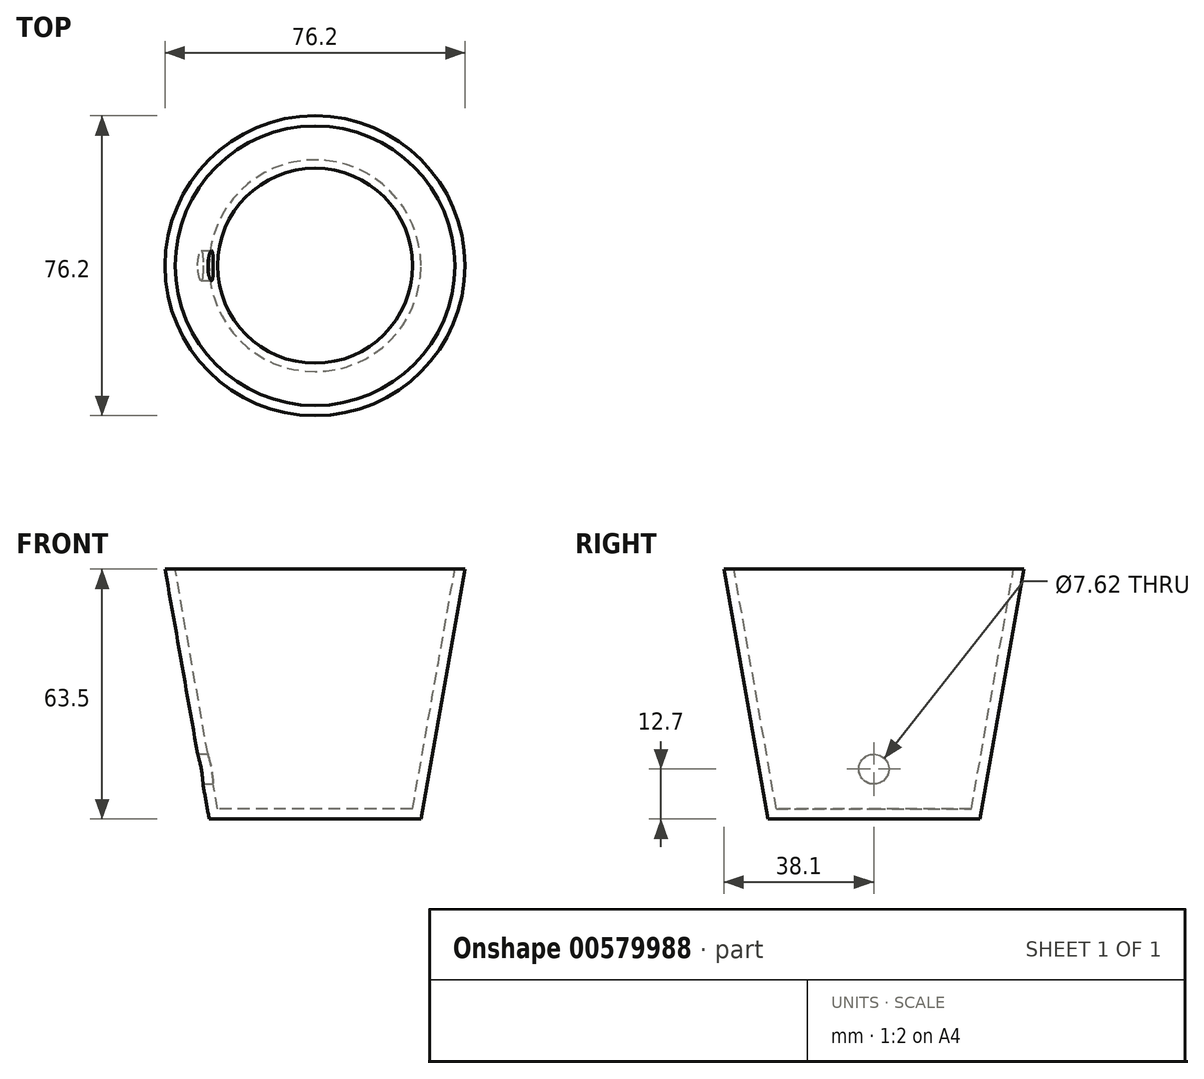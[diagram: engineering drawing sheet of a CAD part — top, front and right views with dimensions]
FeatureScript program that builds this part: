
annotation { "Feature Type Name" : "Feature", "Feature Type Description" : "" }
export const myFeature = defineFeature(function(context is Context, id is Id, definition is map)
    precondition{}
    {
        {
            var Q0;
            Q0=qCreatedBy(makeId("Front.planeOp"),FACE);
            var sketch = newSketch(context, id + "F0", { "sketchPlane" : qUnion([Q0])});
            skLineSegment(sketch, "E0", {"start": v(0, 63.5) * mm, "end": v(-38.1, 63.5) * mm});
            skLineSegment(sketch, "E1", {"start": v(-38.1, 63.5) * mm, "end": v(-26.9, 0) * mm});
            skLineSegment(sketch, "E2", {"start": v(-26.9, 0) * mm, "end": v(0, 0) * mm});
            skLineSegment(sketch, "E3", {"start": v(0, 0) * mm, "end": v(0, 63.5) * mm});
            skSolve(sketch);
        }
        {
            var Q0;
            Q0=makeQuery(id+"F0.imprint","IMPRINT",FACE,{"disambiguationData":[TD([[makeQuery(id+"F0.imprint","IMPRINT",EDGE,{"derivedFrom":sQuery(id+"F0.wireOp",EDGE,"E0")}),1.0]])]});
            var Q1;
            Q1=sQuery(id+"F0.wireOp",EDGE,"E3");
            revolve(context, id + "F1", {"entities" : qUnion([Q0]), "axis" : qUnion([Q1]), "revolveType" : RevolveType.FULL});
        }
        {
            var Q0;
            Q0=makeQuery(id+"F1.opRevolve","SWEPT_FACE",FACE,{"disambiguationData":[OSD([sQuery(id+"F0.wireOp",EDGE,"E0")])]});
            var sketch = newSketch(context, id + "F2", { "sketchPlane" : qUnion([Q0])});
            skCircle(sketch, "E4.0.0", {"center": v(0, 0) * mm, "radius": 38.1 * mm});
            skLineSegment(sketch, "E5", {"start": v(0, -50.8) * mm, "end": v(0, -38.1) * mm, "construction": true});
            skCircle(sketch, "E6", {"center": v(0, -50.8) * mm, "radius": 3.81 * mm});
            skSolve(sketch);
        }
        {
            var Q0;
            Q0=makeQuery(id+"F1.opRevolve","SWEPT_FACE",FACE,{"disambiguationData":[OSD([sQuery(id+"F0.wireOp",EDGE,"E0")])]});
            shell(context, id + "F3", {"entities" : qUnion([Q0]), "thickness" : 2.54 * mm});
        }
        {
            var Q0;
            Q0=qCreatedBy(makeId("Right.planeOp"),FACE);
            var sketch = newSketch(context, id + "F4", { "sketchPlane" : qUnion([Q0])});
            skCircle(sketch, "E7", {"center": v(0, 12.7) * mm, "radius": 3.45 * mm});
            skLineSegment(sketch, "E8", {"start": v(0, 12.7) * mm, "end": v(0, 19.29) * mm, "construction": true});
            skLineSegment(sketch, "E9", {"start": v(0, 12.7) * mm, "end": v(0, 0) * mm, "construction": true});
            skSolve(sketch);
        }
        {
            var Q0;
            Q0=sQuery(id+"F4.wireOp",VERTEX,"E7.center");
            var Q1;
            Q1=makeQuery(id+"F1.opRevolve","SWEPT_BODY",BODY,{"disambiguationData":[OSD([sQuery(id+"F0.wireOp",EDGE,"E0"),sQuery(id+"F0.wireOp",EDGE,"E1"),sQuery(id+"F0.wireOp",EDGE,"E2"),sQuery(id+"F0.wireOp",EDGE,"E3")])]});
            hole(context, id + "F5", {"style" : HoleStyle.SIMPLE, "endStyle" : HoleEndStyle.THROUGH, "holeDiameter" : 7.62 * mm, "isTappedThrough" : true, "tappedDepth" : 12.7 * mm, "tapClearance" : 3, "locations" : qUnion([Q0]), "scope" : qUnion([Q1])});
        }
        {
            var Q0;
            Q0=sQuery(id+"F2.wireOp",VERTEX,"E5.start");
            var Q1;
            Q1=makeQuery(id+"F1.opRevolve","SWEPT_BODY",BODY,{"disambiguationData":[OSD([sQuery(id+"F0.wireOp",EDGE,"E0"),sQuery(id+"F0.wireOp",EDGE,"E1"),sQuery(id+"F0.wireOp",EDGE,"E2"),sQuery(id+"F0.wireOp",EDGE,"E3")])]});
            hole(context, id + "F6", {"style" : HoleStyle.SIMPLE, "endStyle" : HoleEndStyle.THROUGH, "holeDiameter" : 6.35 * mm, "isTappedThrough" : true, "tappedDepth" : 12.7 * mm, "tapClearance" : 3, "locations" : qUnion([Q0]), "scope" : qUnion([Q1])});
        }
    });
